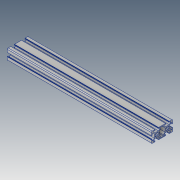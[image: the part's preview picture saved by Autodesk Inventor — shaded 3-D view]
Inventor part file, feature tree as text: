
AUTODESK INVENTOR PART (.ipt)
format: ipt  version: 2018.2 (Build 222227000, 227)  size: 226,816 bytes
history: native  units: mm
features: other x1, extrude x1, sketch x1
ambient origin geometry x8: Origin, YZ Plane, XZ Plane, XY Plane, X Axis, Y Axis, Z Axis, Center Point
bodies: Body1 (feature_tree)
feature tree (3):
  other  "90-50-PROFILES-20x40xSketch.ipt"
  extrude  "Extrusion4"  Depth=270.0mm TaperAngle=0.0deg
  sketch  "Skizze2"  dims[d9=10.0mm d10=270.0mm d11=0.0mm]
